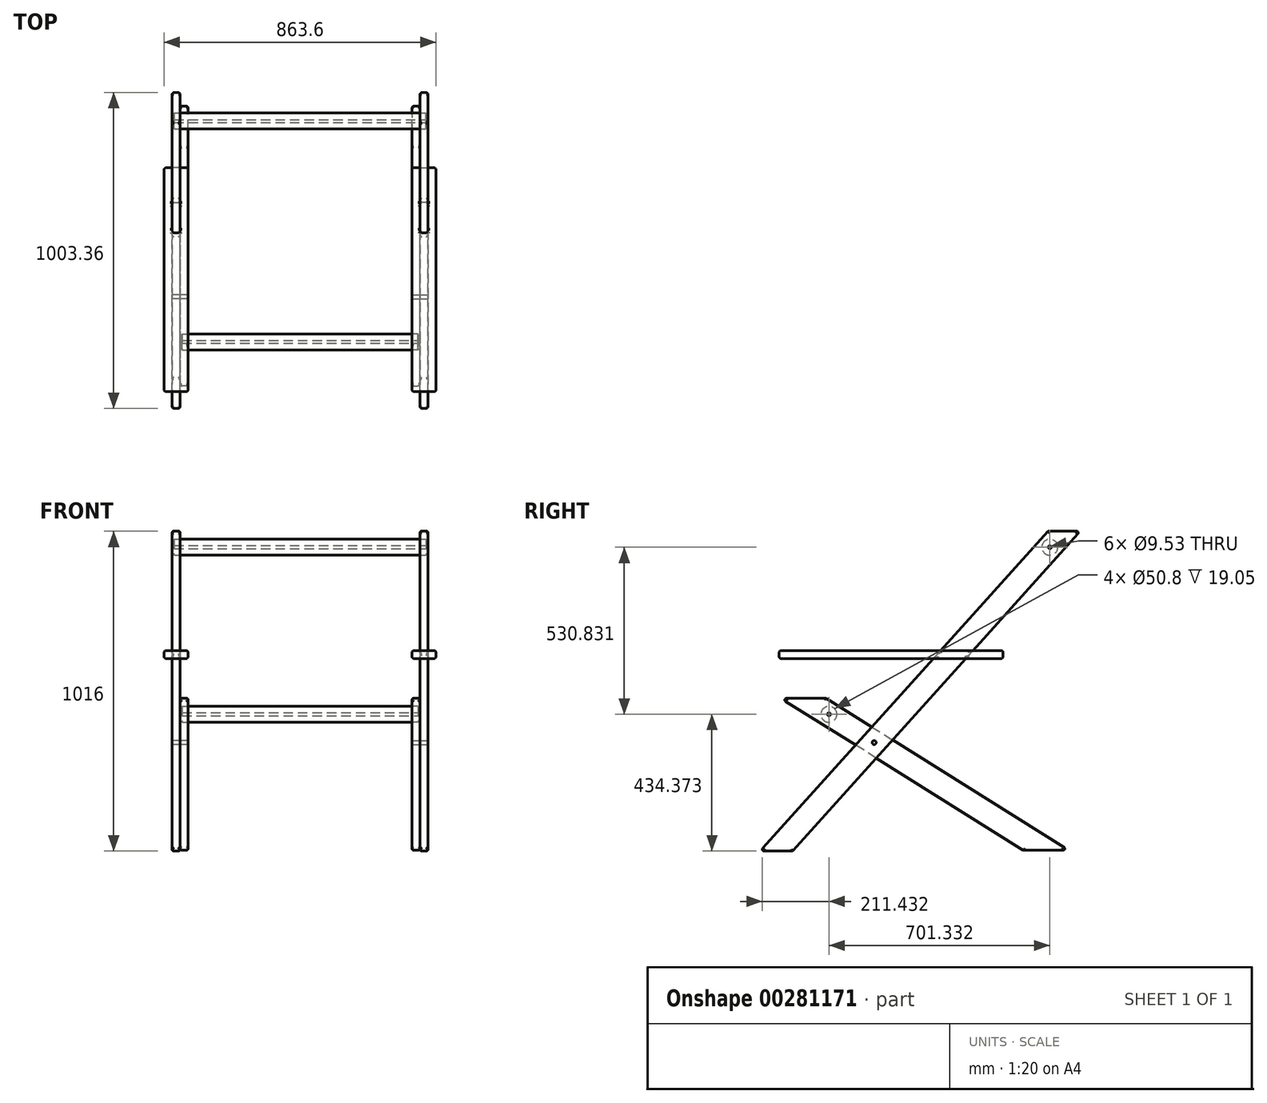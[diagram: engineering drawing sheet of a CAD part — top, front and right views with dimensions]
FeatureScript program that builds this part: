
annotation { "Feature Type Name" : "Feature", "Feature Type Description" : "" }
export const myFeature = defineFeature(function(context is Context, id is Id, definition is map)
    precondition{}
    {
        {
            var Q0;
            Q0=qCreatedBy(makeId("Right.planeOp"),FACE);
            var sketch = newSketch(context, id + "F0", { "sketchPlane" : qUnion([Q0])});
            skLineSegment(sketch, "E0", {"start": v(-674.08, 176.77) * mm, "end": v(-530.49, 176.77) * mm});
            skLineSegment(sketch, "E1", {"start": v(-530.49, 176.77) * mm, "end": v(240.32, -305.83) * mm});
            skLineSegment(sketch, "E2", {"start": v(240.32, -305.83) * mm, "end": v(96.73, -305.83) * mm});
            skLineSegment(sketch, "E3", {"start": v(96.73, -305.83) * mm, "end": v(-674.08, 176.77) * mm});
            skLineSegment(sketch, "E4", {"start": v(-738.9, -308.4) * mm, "end": v(-636.43, -308.4) * mm});
            skLineSegment(sketch, "E5", {"start": v(-636.43, -308.4) * mm, "end": v(277.1, 707.6) * mm});
            skLineSegment(sketch, "E6", {"start": v(277.1, 707.6) * mm, "end": v(174.62, 707.6) * mm});
            skLineSegment(sketch, "E7", {"start": v(174.62, 707.6) * mm, "end": v(-738.9, -308.4) * mm});
            skSolve(sketch);
        }
        {
            var Q0;
            {var subQ5=sQuery(id+"F0.wireOp",EDGE,"E6");Q0=makeQuery(id+"F0.imprint","IMPRINT",FACE,{"disambiguationData":[TD([[makeQuery(id+"F0.imprint","IMPRINT",EDGE,{"derivedFrom":subQ5}),1.0]])]});}
            var Q1;
            {var subQ0=sQuery(id+"F0.wireOp",EDGE,"E7");var subQ1=sQuery(id+"F0.wireOp",EDGE,"E1");var subQ2=makeQuery(id+"F0.imprint","INTERSECT",VERTEX,{"derivedFrom":[subQ1,subQ0]});Q1=makeQuery(id+"F0.imprint","IMPRINT",FACE,{"disambiguationData":[TD([[makeQuery(id+"F0.imprint","IMPRINT",EDGE,{"disambiguationData":[TD([[subQ2,-1.0]])],"derivedFrom":subQ1}),-1.0]])]});}
            var Q2;
            {var subQ5=sQuery(id+"F0.wireOp",EDGE,"E4");Q2=makeQuery(id+"F0.imprint","IMPRINT",FACE,{"disambiguationData":[TD([[makeQuery(id+"F0.imprint","IMPRINT",EDGE,{"derivedFrom":subQ5}),1.0]])]});}
            extrude(context, id + "F1", {"entities" : qUnion([Q0, Q1, Q2]), "depth" : 25.4 * mm});
        }
        {
            var Q0;
            {var subQ0=sQuery(id+"F0.wireOp",EDGE,"E2");Q0=makeQuery(id+"F0.imprint","IMPRINT",FACE,{"disambiguationData":[TD([[makeQuery(id+"F0.imprint","IMPRINT",EDGE,{"derivedFrom":subQ0}),-1.0]])]});}
            var Q1;
            {var subQ0=sQuery(id+"F0.wireOp",EDGE,"E7");var subQ1=sQuery(id+"F0.wireOp",EDGE,"E1");var subQ2=makeQuery(id+"F0.imprint","INTERSECT",VERTEX,{"derivedFrom":[subQ1,subQ0]});Q1=makeQuery(id+"F0.imprint","IMPRINT",FACE,{"disambiguationData":[TD([[makeQuery(id+"F0.imprint","IMPRINT",EDGE,{"disambiguationData":[TD([[subQ2,-1.0]])],"derivedFrom":subQ1}),-1.0]])]});}
            var Q2;
            {var subQ0=sQuery(id+"F0.wireOp",EDGE,"E0");Q2=makeQuery(id+"F0.imprint","IMPRINT",FACE,{"disambiguationData":[TD([[makeQuery(id+"F0.imprint","IMPRINT",EDGE,{"derivedFrom":subQ0}),-1.0]])]});}
            extrude(context, id + "F2", {"entities" : qUnion([Q0, Q1, Q2]), "oppositeDirection" : true, "depth" : 25.4 * mm});
        }
        {
            var Q0;
            Q0=makeQuery(id+"F2.opExtrude","CAP_EDGE",EDGE,{"disambiguationData":[OSD([sQuery(id+"F0.wireOp",EDGE,"E1")])],"isStart":true});
            var Q1;
            Q1=makeQuery(id+"F2.opExtrude","CAP_EDGE",EDGE,{"disambiguationData":[OSD([sQuery(id+"F0.wireOp",EDGE,"E1")])],"isStart":false});
            var Q2;
            Q2=makeQuery(id+"F2.opExtrude","CAP_EDGE",EDGE,{"disambiguationData":[OSD([sQuery(id+"F0.wireOp",EDGE,"E3")])],"isStart":true});
            var Q3;
            Q3=makeQuery(id+"F2.opExtrude","CAP_EDGE",EDGE,{"disambiguationData":[OSD([sQuery(id+"F0.wireOp",EDGE,"E3")])],"isStart":false});
            var Q4;
            Q4=makeQuery(id+"F1.opExtrude","CAP_EDGE",EDGE,{"disambiguationData":[OSD([sQuery(id+"F0.wireOp",EDGE,"E7")])],"isStart":true});
            var Q5;
            Q5=makeQuery(id+"F1.opExtrude","CAP_EDGE",EDGE,{"disambiguationData":[OSD([sQuery(id+"F0.wireOp",EDGE,"E5")])],"isStart":true});
            var Q6;
            Q6=makeQuery(id+"F1.opExtrude","CAP_EDGE",EDGE,{"disambiguationData":[OSD([sQuery(id+"F0.wireOp",EDGE,"E7")])],"isStart":false});
            var Q7;
            Q7=makeQuery(id+"F1.opExtrude","CAP_EDGE",EDGE,{"disambiguationData":[OSD([sQuery(id+"F0.wireOp",EDGE,"E5")])],"isStart":false});
            fillet(context, id + "F3", {"entities" : qUnion([Q0, Q1, Q2, Q3, Q4, Q5, Q6, Q7]), "radius" : 6.35 * mm, "tangentPropagation" : true, "allowEdgeOverflow" : false});
        }
        {
            var Q0;
            Q0=makeQuery(id+"F2.opExtrude","SWEPT_EDGE",EDGE,{"disambiguationData":[OSD([sQuery(id+"F0.wireOp",EDGE,"E0"),sQuery(id+"F0.wireOp",EDGE,"E3")])]});
            var Q1;
            Q1=makeQuery(id+"F2.opExtrude","SWEPT_EDGE",EDGE,{"disambiguationData":[OSD([sQuery(id+"F0.wireOp",EDGE,"E0"),sQuery(id+"F0.wireOp",EDGE,"E1")])]});
            var Q2;
            Q2=makeQuery(id+"F2.opExtrude","SWEPT_EDGE",EDGE,{"disambiguationData":[OSD([sQuery(id+"F0.wireOp",EDGE,"E1"),sQuery(id+"F0.wireOp",EDGE,"E2")])]});
            var Q3;
            Q3=makeQuery(id+"F1.opExtrude","SWEPT_FACE",FACE,{"disambiguationData":[OSD([sQuery(id+"F0.wireOp",EDGE,"E6")])]});
            var Q4;
            Q4=makeQuery(id+"F1.opExtrude","SWEPT_FACE",FACE,{"disambiguationData":[OSD([sQuery(id+"F0.wireOp",EDGE,"E4")])]});
            fillet(context, id + "F4", {"entities" : qUnion([Q0, Q1, Q2, Q3, Q4]), "radius" : 5.08 * mm, "tangentPropagation" : true, "allowEdgeOverflow" : false});
        }
        {
            var Q0;
            Q0=makeQuery(id+"F1.opExtrude","CAP_FACE",FACE,{"disambiguationData":[OSD([sQuery(id+"F0.wireOp",EDGE,"E4"),sQuery(id+"F0.wireOp",EDGE,"E5"),sQuery(id+"F0.wireOp",EDGE,"E6"),sQuery(id+"F0.wireOp",EDGE,"E7")])],"isStart":false});
            var sketch = newSketch(context, id + "F5", { "sketchPlane" : qUnion([Q0])});
            skLineSegment(sketch, "E8.0", {"start": v(-654, 176.77) * mm, "end": v(-534.34, 176.77) * mm});
            skLineSegment(sketch, "E9.0", {"start": v(-731.28, -299.92) * mm, "end": v(173.11, 705.92) * mm});
            skLineSegment(sketch, "E10.0", {"start": v(269.48, 699.13) * mm, "end": v(-634.92, -306.71) * mm});
            skLineSegment(sketch, "E11", {"start": v(-679.4, 302.94) * mm, "end": v(31.8, 302.94) * mm});
            skLineSegment(sketch, "E12", {"start": v(31.8, 302.94) * mm, "end": v(31.8, 328.34) * mm});
            skLineSegment(sketch, "E13", {"start": v(31.8, 328.34) * mm, "end": v(-679.4, 328.34) * mm});
            skLineSegment(sketch, "E14", {"start": v(-679.4, 328.34) * mm, "end": v(-679.4, 302.94) * mm});
            skSolve(sketch);
        }
        {
            var Q0;
            Q0 = qSketchRegion(id + "F5", true);
            extrude(context, id + "F6", {"entities" : qUnion([Q0]), "oppositeDirection" : true, "depth" : 50.8 * mm});
        }
        {
            var Q0;
            Q0 = qSketchRegion(id + "F5", true);
            extrude(context, id + "F7", {"entities" : qUnion([Q0]), "depth" : 25.4 * mm});
        }
        {
            var Q0;
            Q0=makeQuery(id+"F6.opExtrude","SWEPT_BODY",BODY,{"disambiguationData":[OSD([sQuery(id+"F5.wireOp",EDGE,"E11"),sQuery(id+"F5.wireOp",EDGE,"E12"),sQuery(id+"F5.wireOp",EDGE,"E13"),sQuery(id+"F5.wireOp",EDGE,"E14")])]});
            var Q1;
            Q1=makeQuery(id+"F7.opExtrude","SWEPT_BODY",BODY,{"disambiguationData":[OSD([sQuery(id+"F5.wireOp",EDGE,"E11"),sQuery(id+"F5.wireOp",EDGE,"E12"),sQuery(id+"F5.wireOp",EDGE,"E13"),sQuery(id+"F5.wireOp",EDGE,"E14")])]});
            booleanBodies(context, id + "F8", {"operationType" : BooleanOperationType.UNION, "tools" : qUnion([Q0, Q1])});
        }
        {
            var Q0;
            Q0=makeQuery(id+"F1.opExtrude","SWEPT_BODY",BODY,{"disambiguationData":[OSD([sQuery(id+"F0.wireOp",EDGE,"E4"),sQuery(id+"F0.wireOp",EDGE,"E5"),sQuery(id+"F0.wireOp",EDGE,"E6"),sQuery(id+"F0.wireOp",EDGE,"E7")])]});
            var Q1;
            Q1=makeQuery(id+"F6.opExtrude","SWEPT_BODY",BODY,{"disambiguationData":[OSD([sQuery(id+"F5.wireOp",EDGE,"E11"),sQuery(id+"F5.wireOp",EDGE,"E12"),sQuery(id+"F5.wireOp",EDGE,"E13"),sQuery(id+"F5.wireOp",EDGE,"E14")])]});
            var Q2;
            Q2=makeQuery(id+"F1.opExtrude","CAP_FACE",FACE,{"disambiguationData":[OSD([sQuery(id+"F0.wireOp",EDGE,"E4"),sQuery(id+"F0.wireOp",EDGE,"E5"),sQuery(id+"F0.wireOp",EDGE,"E6"),sQuery(id+"F0.wireOp",EDGE,"E7")])],"isStart":false});
            var Q3;
            {var subQ0=sQuery(id+"F0.wireOp",EDGE,"E5");Q3=makeQuery(id+"F3.opFillet","BLEND_FACE",FACE,{"disambiguationData":[OSD([subQ0]),TDD([makeQuery(id+"F1.opExtrude","CAP_EDGE",EDGE,{"disambiguationData":[OSD([subQ0])],"isStart":false})])]});}
            var Q4;
            Q4=makeQuery(id+"F1.opExtrude","SWEPT_FACE",FACE,{"disambiguationData":[OSD([sQuery(id+"F0.wireOp",EDGE,"E5")])]});
            var Q5;
            {var subQ0=sQuery(id+"F0.wireOp",EDGE,"E5");Q5=makeQuery(id+"F3.opFillet","BLEND_FACE",FACE,{"disambiguationData":[OSD([subQ0]),TDD([makeQuery(id+"F1.opExtrude","CAP_EDGE",EDGE,{"disambiguationData":[OSD([subQ0])],"isStart":true})])]});}
            var Q6;
            Q6=makeQuery(id+"F1.opExtrude","CAP_FACE",FACE,{"disambiguationData":[OSD([sQuery(id+"F0.wireOp",EDGE,"E4"),sQuery(id+"F0.wireOp",EDGE,"E5"),sQuery(id+"F0.wireOp",EDGE,"E6"),sQuery(id+"F0.wireOp",EDGE,"E7")])],"isStart":true});
            var Q7;
            {var subQ0=sQuery(id+"F0.wireOp",EDGE,"E7");Q7=makeQuery(id+"F3.opFillet","BLEND_FACE",FACE,{"disambiguationData":[OSD([subQ0]),TDD([makeQuery(id+"F1.opExtrude","CAP_EDGE",EDGE,{"disambiguationData":[OSD([subQ0])],"isStart":true})])]});}
            var Q8;
            Q8=makeQuery(id+"F1.opExtrude","SWEPT_FACE",FACE,{"disambiguationData":[OSD([sQuery(id+"F0.wireOp",EDGE,"E7")])]});
            var Q9;
            {var subQ0=sQuery(id+"F0.wireOp",EDGE,"E7");Q9=makeQuery(id+"F3.opFillet","BLEND_FACE",FACE,{"disambiguationData":[OSD([subQ0]),TDD([makeQuery(id+"F1.opExtrude","CAP_EDGE",EDGE,{"disambiguationData":[OSD([subQ0])],"isStart":false})])]});}
            booleanBodies(context, id + "F9", {"operationType" : BooleanOperationType.SUBTRACTION, "tools" : qUnion([Q0]), "targets" : qUnion([Q1]), "offset" : true, "entitiesToOffset" : qUnion([Q2, Q3, Q4, Q5, Q6, Q7, Q8, Q9]), "offsetDistance" : 0.25 * mm, "keepTools" : true});
        }
        {
            var Q0;
            {var subQ0=sQuery(id+"F5.wireOp",EDGE,"E13");Q0=makeQuery(id+"F9.tempBoolean.opBoolean","INTERSECT",EDGE,{"derivedFrom":[makeQuery(id+"F8.opBoolean","MERGE",FACE,{"derivedFrom":[makeQuery(id+"F6.opExtrude","SWEPT_FACE",FACE,{"disambiguationData":[OSD([subQ0])]}),makeQuery(id+"F7.opExtrude","SWEPT_FACE",FACE,{"disambiguationData":[OSD([subQ0])]})]}),makeQuery(id+"F9.offsetTempBody.opPattern","COPY",FACE,{"derivedFrom":makeQuery(id+"F1.opExtrude","CAP_FACE",FACE,{"disambiguationData":[OSD([sQuery(id+"F0.wireOp",EDGE,"E4"),sQuery(id+"F0.wireOp",EDGE,"E5"),sQuery(id+"F0.wireOp",EDGE,"E6"),sQuery(id+"F0.wireOp",EDGE,"E7")])],"isStart":false}),"instanceName":"1"})]});}
            var Q1;
            {var subQ0=sQuery(id+"F5.wireOp",EDGE,"E11");Q1=makeQuery(id+"F9.tempBoolean.opBoolean","INTERSECT",EDGE,{"derivedFrom":[makeQuery(id+"F8.opBoolean","MERGE",FACE,{"derivedFrom":[makeQuery(id+"F6.opExtrude","SWEPT_FACE",FACE,{"disambiguationData":[OSD([subQ0])]}),makeQuery(id+"F7.opExtrude","SWEPT_FACE",FACE,{"disambiguationData":[OSD([subQ0])]})]}),makeQuery(id+"F9.offsetTempBody.opPattern","COPY",FACE,{"derivedFrom":makeQuery(id+"F1.opExtrude","SWEPT_FACE",FACE,{"disambiguationData":[OSD([sQuery(id+"F0.wireOp",EDGE,"E5")])]}),"instanceName":"1"})]});}
            fillet(context, id + "F10", {"entities" : qUnion([Q0, Q1]), "radius" : 6.35 * mm, "tangentPropagation" : true, "allowEdgeOverflow" : false});
        }
        {
            var Q0;
            Q0=makeQuery(id+"F7.opExtrude","CAP_EDGE",EDGE,{"disambiguationData":[OSD([sQuery(id+"F5.wireOp",EDGE,"E13")])],"isStart":false});
            var Q1;
            Q1=makeQuery(id+"F7.opExtrude","CAP_EDGE",EDGE,{"disambiguationData":[OSD([sQuery(id+"F5.wireOp",EDGE,"E11")])],"isStart":false});
            var Q2;
            {var subQ0=sQuery(id+"F5.wireOp",EDGE,"E14");Q2=makeQuery(id+"F8.opBoolean","MERGE",FACE,{"derivedFrom":[makeQuery(id+"F6.opExtrude","SWEPT_FACE",FACE,{"disambiguationData":[OSD([subQ0])]}),makeQuery(id+"F7.opExtrude","SWEPT_FACE",FACE,{"disambiguationData":[OSD([subQ0])]})]});}
            var Q3;
            Q3=makeQuery(id+"F6.opExtrude","CAP_FACE",FACE,{"disambiguationData":[OSD([sQuery(id+"F5.wireOp",EDGE,"E11"),sQuery(id+"F5.wireOp",EDGE,"E12"),sQuery(id+"F5.wireOp",EDGE,"E13"),sQuery(id+"F5.wireOp",EDGE,"E14")])],"isStart":false});
            var Q4;
            {var subQ0=sQuery(id+"F5.wireOp",EDGE,"E12");Q4=makeQuery(id+"F8.opBoolean","MERGE",FACE,{"derivedFrom":[makeQuery(id+"F6.opExtrude","SWEPT_FACE",FACE,{"disambiguationData":[OSD([subQ0])]}),makeQuery(id+"F7.opExtrude","SWEPT_FACE",FACE,{"disambiguationData":[OSD([subQ0])]})]});}
            fillet(context, id + "F11", {"entities" : qUnion([Q0, Q1, Q2, Q3, Q4]), "radius" : 6.35 * mm, "tangentPropagation" : true, "allowEdgeOverflow" : false});
        }
        {
            var Q0;
            Q0=makeQuery(id+"F1.opExtrude","CAP_FACE",FACE,{"disambiguationData":[OSD([sQuery(id+"F0.wireOp",EDGE,"E4"),sQuery(id+"F0.wireOp",EDGE,"E5"),sQuery(id+"F0.wireOp",EDGE,"E6"),sQuery(id+"F0.wireOp",EDGE,"E7")])],"isStart":true});
            var sketch = newSketch(context, id + "F12", { "sketchPlane" : qUnion([Q0])});
            skCircle(sketch, "E15", {"center": v(-180.18, 656.8) * mm, "radius": 25.4 * mm});
            skSolve(sketch);
        }
        {
            var Q0;
            Q0=makeQuery(id+"F12.imprint","IMPRINT",FACE,{"disambiguationData":[TD([[makeQuery(id+"F12.imprint","IMPRINT",EDGE,{"derivedFrom":sQuery(id+"F12.wireOp",EDGE,"E15")}),1.0]])]});
            extrude(context, id + "F13", {"entities" : qUnion([Q0]), "operationType" : NewBodyOperationType.REMOVE, "oppositeDirection" : true, "depth" : 19.05 * mm});
        }
        {
            var Q0;
            Q0=makeQuery(id+"F2.opExtrude","CAP_FACE",FACE,{"disambiguationData":[OSD([sQuery(id+"F0.wireOp",EDGE,"E0"),sQuery(id+"F0.wireOp",EDGE,"E1"),sQuery(id+"F0.wireOp",EDGE,"E2"),sQuery(id+"F0.wireOp",EDGE,"E3")])],"isStart":false});
            var sketch = newSketch(context, id + "F14", { "sketchPlane" : qUnion([Q0])});
            skCircle(sketch, "E16", {"center": v(521.15, 125.97) * mm, "radius": 25.4 * mm});
            skSolve(sketch);
        }
        {
            var Q0;
            Q0=makeQuery(id+"F14.imprint","IMPRINT",FACE,{"disambiguationData":[TD([[makeQuery(id+"F14.imprint","IMPRINT",EDGE,{"derivedFrom":sQuery(id+"F14.wireOp",EDGE,"E16")}),1.0]])]});
            extrude(context, id + "F15", {"entities" : qUnion([Q0]), "operationType" : NewBodyOperationType.REMOVE, "oppositeDirection" : true, "depth" : 19.05 * mm});
        }
        {
            var Q0;
            Q0=makeQuery(id+"F1.opExtrude","CAP_FACE",FACE,{"disambiguationData":[OSD([sQuery(id+"F0.wireOp",EDGE,"E4"),sQuery(id+"F0.wireOp",EDGE,"E5"),sQuery(id+"F0.wireOp",EDGE,"E6"),sQuery(id+"F0.wireOp",EDGE,"E7")])],"isStart":false});
            var sketch = newSketch(context, id + "F16", { "sketchPlane" : qUnion([Q0])});
            skPoint(sketch, "E17", {"position": v(-377.63, 36.12) * mm});
            skSolve(sketch);
        }
        {
            var Q0;
            Q0=sQuery(id+"F16.wireOp",VERTEX,"E17");
            var Q1;
            Q1=makeQuery(id+"F1.opExtrude","SWEPT_BODY",BODY,{"disambiguationData":[OSD([sQuery(id+"F0.wireOp",EDGE,"E4"),sQuery(id+"F0.wireOp",EDGE,"E5"),sQuery(id+"F0.wireOp",EDGE,"E6"),sQuery(id+"F0.wireOp",EDGE,"E7")])]});
            var Q2;
            Q2=makeQuery(id+"F2.opExtrude","SWEPT_BODY",BODY,{"disambiguationData":[OSD([sQuery(id+"F0.wireOp",EDGE,"E0"),sQuery(id+"F0.wireOp",EDGE,"E1"),sQuery(id+"F0.wireOp",EDGE,"E2"),sQuery(id+"F0.wireOp",EDGE,"E3")])]});
            hole(context, id + "F17", {"style" : HoleStyle.SIMPLE, "endStyle" : HoleEndStyle.THROUGH, "holeDiameter" : 12.7 * mm, "tappedDepth" : 12.7 * mm, "tapClearance" : 3, "locations" : qUnion([Q0]), "scope" : qUnion([Q1, Q2])});
        }
        {
            var Q0;
            Q0=makeQuery(id+"F1.opExtrude","CAP_FACE",FACE,{"disambiguationData":[OSD([sQuery(id+"F0.wireOp",EDGE,"E4"),sQuery(id+"F0.wireOp",EDGE,"E5"),sQuery(id+"F0.wireOp",EDGE,"E6"),sQuery(id+"F0.wireOp",EDGE,"E7")])],"isStart":false});
            var sketch = newSketch(context, id + "F18", { "sketchPlane" : qUnion([Q0])});
            skCircle(sketch, "E18.0", {"center": v(180.18, 656.8) * mm, "radius": 25.4 * mm});
            skSolve(sketch);
        }
        {
            var Q0;
            Q0=sQuery(id+"F18.wireOp",VERTEX,"E18.0.center");
            var Q1;
            Q1=makeQuery(id+"F1.opExtrude","SWEPT_BODY",BODY,{"disambiguationData":[OSD([sQuery(id+"F0.wireOp",EDGE,"E4"),sQuery(id+"F0.wireOp",EDGE,"E5"),sQuery(id+"F0.wireOp",EDGE,"E6"),sQuery(id+"F0.wireOp",EDGE,"E7")])]});
            hole(context, id + "F19", {"style" : HoleStyle.SIMPLE, "endStyle" : HoleEndStyle.THROUGH, "holeDiameter" : 9.52 * mm, "tappedDepth" : 12.7 * mm, "tapClearance" : 3, "locations" : qUnion([Q0]), "scope" : qUnion([Q1])});
        }
        {
            var Q0;
            Q0=makeQuery(id+"F2.opExtrude","CAP_FACE",FACE,{"disambiguationData":[OSD([sQuery(id+"F0.wireOp",EDGE,"E0"),sQuery(id+"F0.wireOp",EDGE,"E1"),sQuery(id+"F0.wireOp",EDGE,"E2"),sQuery(id+"F0.wireOp",EDGE,"E3")])],"isStart":true});
            var sketch = newSketch(context, id + "F20", { "sketchPlane" : qUnion([Q0])});
            skCircle(sketch, "E19.0", {"center": v(-521.15, 125.97) * mm, "radius": 25.4 * mm});
            skSolve(sketch);
        }
        {
            var Q0;
            Q0=sQuery(id+"F20.wireOp",VERTEX,"E19.0.center");
            var Q1;
            Q1=makeQuery(id+"F2.opExtrude","SWEPT_BODY",BODY,{"disambiguationData":[OSD([sQuery(id+"F0.wireOp",EDGE,"E0"),sQuery(id+"F0.wireOp",EDGE,"E1"),sQuery(id+"F0.wireOp",EDGE,"E2"),sQuery(id+"F0.wireOp",EDGE,"E3")])]});
            hole(context, id + "F21", {"style" : HoleStyle.SIMPLE, "endStyle" : HoleEndStyle.THROUGH, "holeDiameter" : 9.52 * mm, "tappedDepth" : 12.7 * mm, "tapClearance" : 3, "locations" : qUnion([Q0]), "scope" : qUnion([Q1])});
        }
        {
            var Q0;
            Q0=makeQuery(id+"F13.boolean.opBoolean","COPY",FACE,{"derivedFrom":makeQuery(id+"F13.opExtrude","CAP_FACE",FACE,{"disambiguationData":[OSD([sQuery(id+"F12.wireOp",EDGE,"E15")])],"isStart":false})});
            extrude(context, id + "F22", {"entities" : qUnion([Q0]), "depth" : 800.1 * mm});
        }
        {
            var Q0;
            Q0=makeQuery(id+"F15.boolean.opBoolean","COPY",FACE,{"derivedFrom":makeQuery(id+"F15.opExtrude","CAP_FACE",FACE,{"disambiguationData":[OSD([sQuery(id+"F14.wireOp",EDGE,"E16")])],"isStart":false})});
            extrude(context, id + "F23", {"entities" : qUnion([Q0]), "depth" : 749.3 * mm});
        }
        {
            var Q0;
            Q0=makeQuery(id+"F1.opExtrude","CAP_FACE",FACE,{"disambiguationData":[OSD([sQuery(id+"F0.wireOp",EDGE,"E4"),sQuery(id+"F0.wireOp",EDGE,"E5"),sQuery(id+"F0.wireOp",EDGE,"E6"),sQuery(id+"F0.wireOp",EDGE,"E7")])],"isStart":true});
            cPlane(context, id + "F24", {"entities" : qUnion([Q0]), "cplaneType" : CPlaneType.OFFSET, "offset" : 381 * mm, "width" : 152.4 * mm, "height" : 152.4 * mm});
        }
        {
            var Q0;
            Q0=makeQuery(id+"F1.opExtrude","SWEPT_BODY",BODY,{"disambiguationData":[OSD([sQuery(id+"F0.wireOp",EDGE,"E4"),sQuery(id+"F0.wireOp",EDGE,"E5"),sQuery(id+"F0.wireOp",EDGE,"E6"),sQuery(id+"F0.wireOp",EDGE,"E7")])]});
            var Q1;
            Q1=makeQuery(id+"F2.opExtrude","SWEPT_BODY",BODY,{"disambiguationData":[OSD([sQuery(id+"F0.wireOp",EDGE,"E0"),sQuery(id+"F0.wireOp",EDGE,"E1"),sQuery(id+"F0.wireOp",EDGE,"E2"),sQuery(id+"F0.wireOp",EDGE,"E3")])]});
            var Q2;
            Q2=makeQuery(id+"F6.opExtrude","SWEPT_BODY",BODY,{"disambiguationData":[OSD([sQuery(id+"F5.wireOp",EDGE,"E11"),sQuery(id+"F5.wireOp",EDGE,"E12"),sQuery(id+"F5.wireOp",EDGE,"E13"),sQuery(id+"F5.wireOp",EDGE,"E14")])]});
            var Q3;
            Q3=qCreatedBy(id+"F24.planeOp",FACE);
            mirror(context, id + "F25", {"entities" : qUnion([Q0, Q1, Q2]), "mirrorPlane" : qUnion([Q3])});
        }
    });
